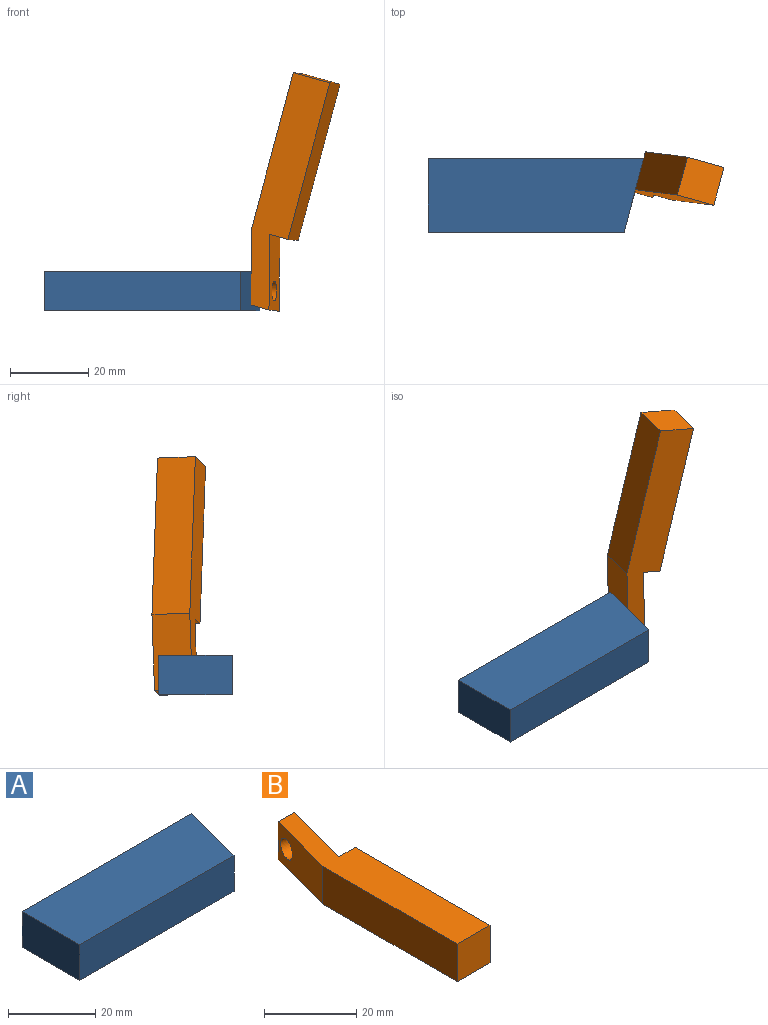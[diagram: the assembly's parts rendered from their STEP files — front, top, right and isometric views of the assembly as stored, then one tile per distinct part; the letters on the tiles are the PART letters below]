
ASSEMBLY  parts=2 mates=1
PART A: 7 faces, bbox 55x23.5x10 mm
  f0: plane 50x10mm, normal (0,-1,0), area 500mm2, adj f1,f3,f4,f5
  f1: plane 18.66x10mm, normal (0.97,-0.26,0), area 173.6mm2, adj f0,f2,f4,f5,f6
  f2: plane 55x10mm, normal (0,1,0), area 474.1mm2, adj f1,f3,f4,f5,f6
  f3: plane 18.66x10mm, normal (-1,0,0), area 186.6mm2, adj f0,f2,f4,f5
  f4: plane 55x18.66mm, normal (0,0,1), area 979.7mm2, adj f0,f1,f2,f3
  f5: plane 55x18.66mm, normal (0,0,-1), area 979.7mm2, adj f0,f1,f2,f3
  f6: cylinder r=2.5mm len=23.79mm, axis (0.97,-0.26,0), area 217.2mm2, adj f1,f2
PART B: 10 faces, bbox 10x60x10 mm
  f0: plane 41.34x10mm, normal (1,0,0), area 413.4mm2, adj f1,f6,f7,f8
  f1: plane 10x5mm, normal (0,1,0), area 50mm2, adj f0,f2,f7,f8
  f2: plane 18.66x10mm, normal (0.97,-0.26,0), area 173.6mm2, adj f1,f3,f7,f8,f9
  f3: plane 10x5mm, normal (0,1,0), area 50mm2, adj f2,f4,f7,f8
  f4: plane 18.66x10mm, normal (-0.97,0.26,0), area 173.6mm2, adj f3,f5,f7,f8,f9
  f5: plane 41.34x10mm, normal (-1,0,0), area 413.4mm2, adj f4,f6,f7,f8
  f6: plane 10x10mm, normal (0,-1,0), area 100mm2, adj f0,f5,f7,f8
  f7: plane 60x10mm, normal (0,0,1), area 506.7mm2, adj f0,f1,f2,f3,f4,f5,f6
  f8: plane 60x10mm, normal (0,0,-1), area 506.7mm2, adj f0,f1,f2,f3,f4,f5,f6
  f9: cylinder r=2.5mm len=6.08mm, axis (0.97,-0.26,0), area 75.9mm2, adj f2,f4
PLACE A t=(-3.66,-2.24,0.31)mm fixed
PLACE B rot(axis=(-0.97,0.26,0),92deg) t=(-5.6,-9.48,3.07)mm
MATE revolute B.f9 <-> A.f6  axis (-0.97,0.26,0) through (0.38,-5.82,5.31)mm
